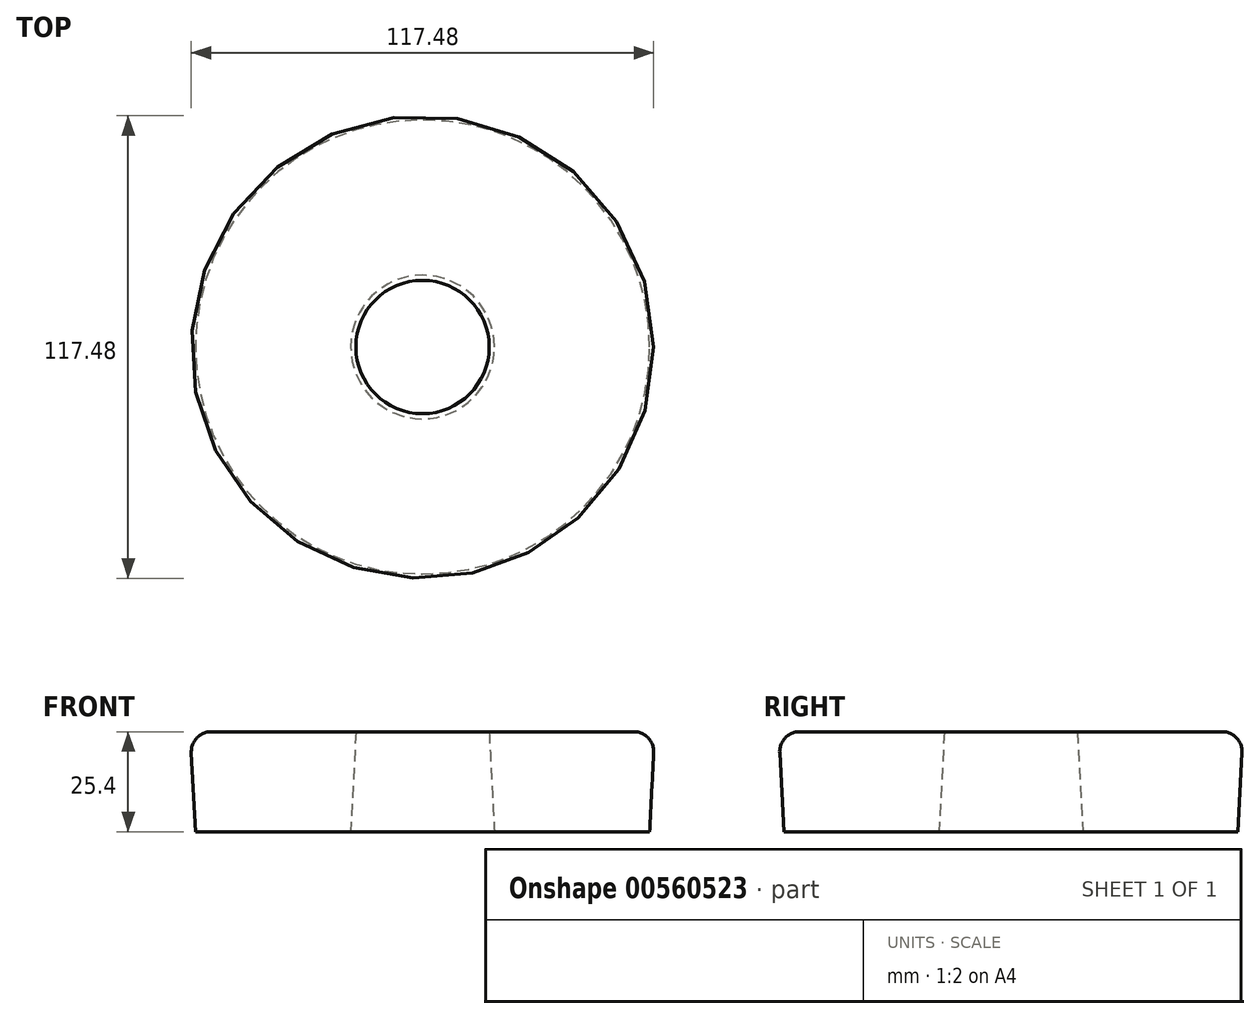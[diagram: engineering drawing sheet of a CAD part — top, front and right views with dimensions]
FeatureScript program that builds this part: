
annotation { "Feature Type Name" : "Feature", "Feature Type Description" : "" }
export const myFeature = defineFeature(function(context is Context, id is Id, definition is map)
    precondition{}
    {
        {
            var Q0;
            Q0=qCreatedBy(makeId("Top.planeOp"),FACE);
            var sketch = newSketch(context, id + "F0", { "sketchPlane" : qUnion([Q0])});
            skCircle(sketch, "E0", {"center": v(0, 0) * mm, "radius": 57.68 * mm});
            skCircle(sketch, "E1", {"center": v(0, 0) * mm, "radius": 18.25 * mm});
            skSolve(sketch);
        }
        {
            var Q0;
            Q0=makeQuery(id+"F0.imprint","IMPRINT",FACE,{"disambiguationData":[TD([[makeQuery(id+"F0.imprint","IMPRINT",EDGE,{"derivedFrom":sQuery(id+"F0.wireOp",EDGE,"E0")}),1.0]])]});
            extrude(context, id + "F1", {"entities" : qUnion([Q0]), "depth" : 25.4 * mm, "offsetDistance" : 25.4 * mm, "hasDraft" : true, "draftAngle" : 3 * degree});
        }
        {
            var Q0;
            Q0=makeQuery(id+"F1.opExtrude","CAP_EDGE",EDGE,{"disambiguationData":[OSD([sQuery(id+"F0.wireOp",EDGE,"E0")])],"isStart":false});
            fillet(context, id + "F2", {"entities" : qUnion([Q0]), "radius" : 5.08 * mm, "tangentPropagation" : true, "allowEdgeOverflow" : false});
        }
    });
